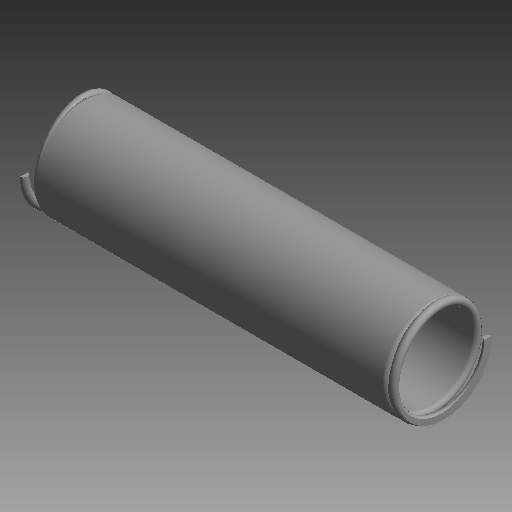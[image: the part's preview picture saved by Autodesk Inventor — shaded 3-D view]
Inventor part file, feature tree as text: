
AUTODESK INVENTOR PART (.ipt)
format: ipt  version: 2019 (Build 230136000, 136)  size: 194,048 bytes
history: native  units: mm (DEFAULTED — no unit token found)
features: revolve x7, sketch x7
ambient origin geometry x8: Origin, YZ Plane, XZ Plane, XY Plane, X Axis, Y Axis, Z Axis, Center Point
bodies: Solid1 (feature_tree)
feature tree (14):
  revolve  "Revolution1"  Angle=180.0deg
  revolve  "Revolution2"  Angle=360.0deg
  revolve  "Revolution3"  Angle=180.0deg
  revolve  "Revolution4"  [1 undecoded]
  revolve  "Revolution5"  [1 undecoded]
  revolve  "Revolution6"  [1 undecoded]
  revolve  "Revolution7"  [1 undecoded]
  sketch  "Sketch_14"  dims[d4=180.0deg d5=180.0deg]
  sketch  "Sketch_5"  dims[d0=180.0deg d1=180.0deg]
  sketch  "Sketch_6"  dims[d2=360.0deg d3=360.0deg]
  sketch  "Sketch_30"
  sketch  "Sketch_18"  dims[d6=360.0deg]
  sketch  "Sketch_19"
  sketch  "Sketch_20"
note: 4 required parameter values undecoded (feature->parameter linkage not recoverable at this tier; creation-order binding heuristic only, values carry confidence <= 0.55)
